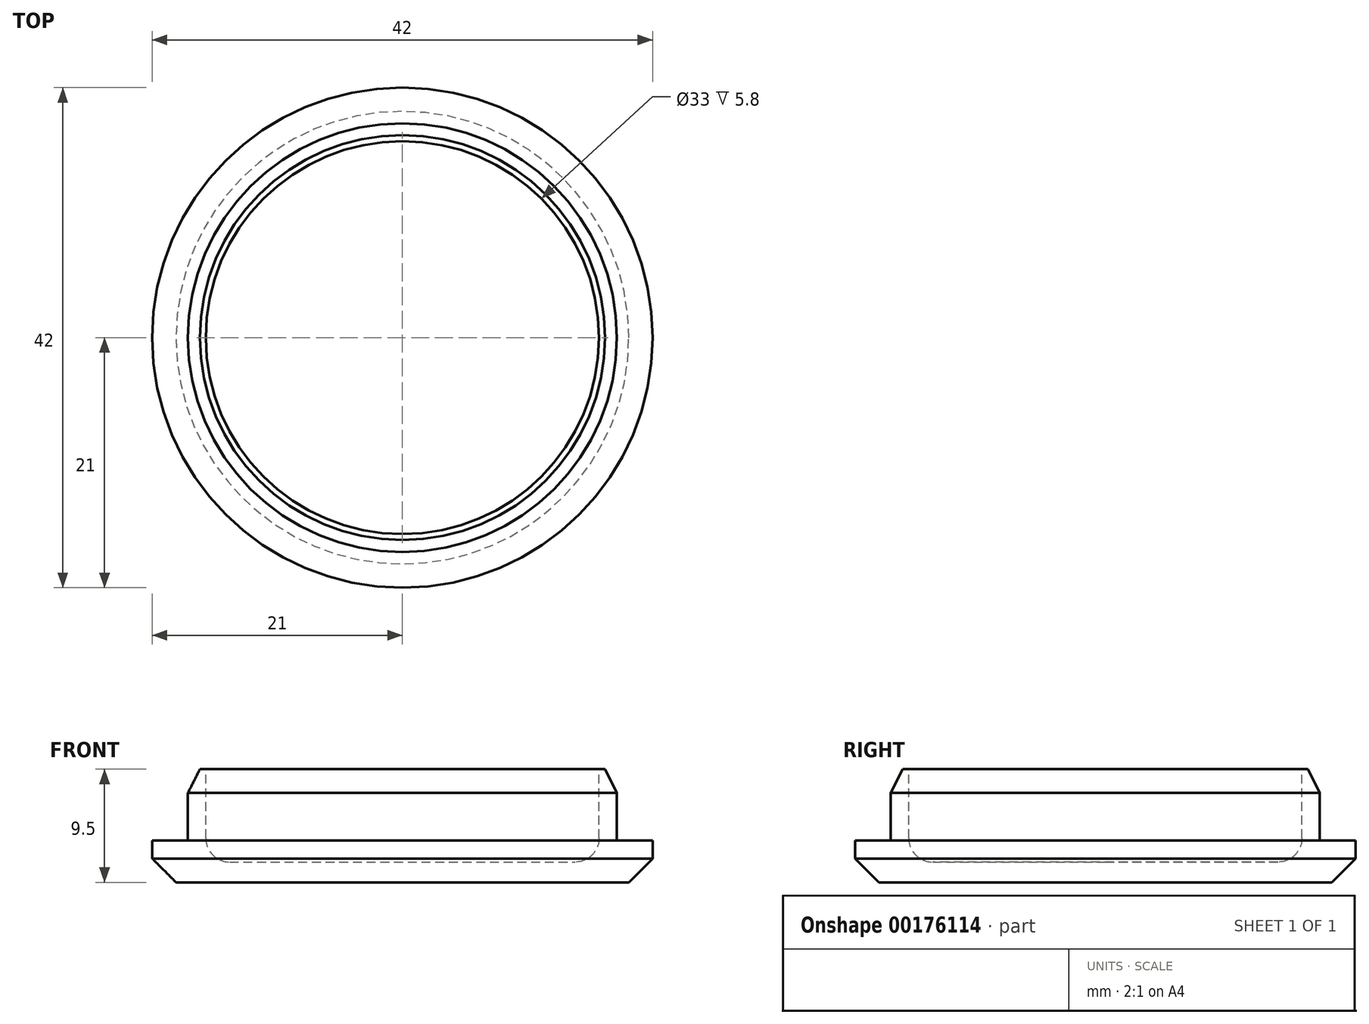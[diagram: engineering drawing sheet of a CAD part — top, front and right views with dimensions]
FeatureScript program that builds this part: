
annotation { "Feature Type Name" : "Feature", "Feature Type Description" : "" }
export const myFeature = defineFeature(function(context is Context, id is Id, definition is map)
    precondition{}
    {
        {
            var Q0;
            Q0=qCreatedBy(makeId("Front.planeOp"),FACE);
            var sketch = newSketch(context, id + "F0", { "sketchPlane" : qUnion([Q0])});
            skLineSegment(sketch, "E0", {"start": v(-21, 3.5) * mm, "end": v(-18, 3.5) * mm});
            skLineSegment(sketch, "E1", {"start": v(-18, 3.5) * mm, "end": v(-18, 9.5) * mm});
            skLineSegment(sketch, "E2", {"start": v(-18, 9.5) * mm, "end": v(-16.5, 9.5) * mm});
            skLineSegment(sketch, "E3", {"start": v(-16.5, 9.5) * mm, "end": v(-16.5, 1.7) * mm});
            skLineSegment(sketch, "E4", {"start": v(-16.5, 1.7) * mm, "end": v(0, 1.7) * mm});
            skLineSegment(sketch, "E5", {"start": v(0, 1.7) * mm, "end": v(0, 0) * mm});
            skLineSegment(sketch, "E6", {"start": v(-21, 3.5) * mm, "end": v(-21, 0) * mm});
            skLineSegment(sketch, "E7", {"start": v(-21, 0) * mm, "end": v(0, 0) * mm});
            skSolve(sketch);
        }
        {
            var Q0;
            Q0=makeQuery(id+"F0.imprint","IMPRINT",FACE,{"disambiguationData":[TD([[makeQuery(id+"F0.imprint","IMPRINT",EDGE,{"derivedFrom":sQuery(id+"F0.wireOp",EDGE,"E0")}),-1.0]])]});
            var Q1;
            Q1=sQuery(id+"F0.wireOp",EDGE,"E5");
            revolve(context, id + "F1", {"surfaceOperationType" : NewSurfaceOperationType.NEW, "entities" : qUnion([Q0]), "axis" : qUnion([Q1]), "revolveType" : RevolveType.FULL});
        }
        {
            var Q0;
            Q0=makeQuery(id+"F1.opRevolve","SWEPT_EDGE",EDGE,{"disambiguationData":[OSD([sQuery(id+"F0.wireOp",EDGE,"E3"),sQuery(id+"F0.wireOp",EDGE,"E4")])]});
            fillet(context, id + "F2", {"entities" : qUnion([Q0]), "tangentPropagation" : true, "radius" : 2 * mm, "defaultsChanged" : false, "vertexSettings" : [], "allowEdgeOverflow" : false});
        }
        {
            var Q0;
            Q0=makeQuery(id+"F1.opRevolve","SWEPT_EDGE",EDGE,{"disambiguationData":[OSD([sQuery(id+"F0.wireOp",EDGE,"E6"),sQuery(id+"F0.wireOp",EDGE,"E7")])]});
            chamfer(context, id + "F3", {"entities" : qUnion([Q0]), "width" : 2 * mm, "tangentPropagation" : true});
        }
        {
            var Q0;
            Q0=makeQuery(id+"F1.opRevolve","SWEPT_EDGE",EDGE,{"disambiguationData":[OSD([sQuery(id+"F0.wireOp",EDGE,"E1"),sQuery(id+"F0.wireOp",EDGE,"E2")])]});
            chamfer(context, id + "F4", {"entities" : qUnion([Q0]), "chamferType" : ChamferType.TWO_OFFSETS, "width1" : 1 * mm, "oppositeDirection" : false, "width2" : 2 * mm, "tangentPropagation" : true});
        }
    });
